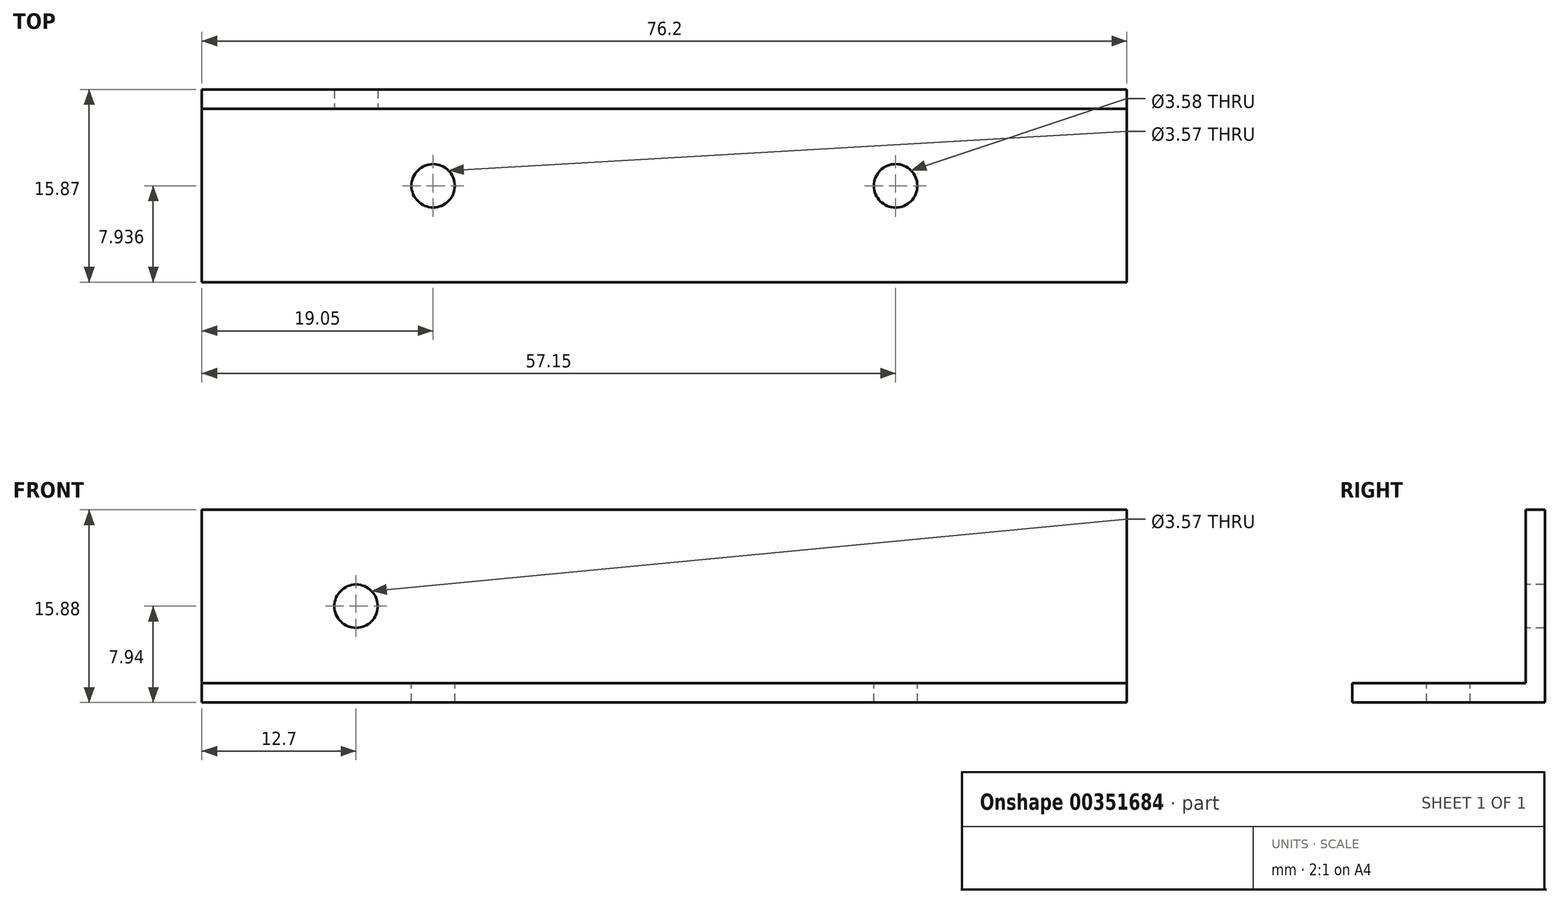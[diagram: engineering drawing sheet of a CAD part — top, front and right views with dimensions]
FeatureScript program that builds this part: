
annotation { "Feature Type Name" : "Feature", "Feature Type Description" : "" }
export const myFeature = defineFeature(function(context is Context, id is Id, definition is map)
    precondition{}
    {
        {
            var Q0;
            Q0=qCreatedBy(makeId("Front.planeOp"),FACE);
            var sketch = newSketch(context, id + "F0", { "sketchPlane" : qUnion([Q0])});
            skLineSegment(sketch, "E0.bottom", {"start": v(-38.1, 7.94) * mm, "end": v(38.1, 7.94) * mm});
            skLineSegment(sketch, "E0.top", {"start": v(-38.1, -7.94) * mm, "end": v(38.1, -7.94) * mm});
            skLineSegment(sketch, "E0.left", {"start": v(-38.1, 7.94) * mm, "end": v(-38.1, -7.94) * mm});
            skLineSegment(sketch, "E0.right", {"start": v(38.1, 7.94) * mm, "end": v(38.1, -7.94) * mm});
            skPoint(sketch, "E0.middle", {"position": v(0, 0) * mm});
            skSolve(sketch);
        }
        {
            var Q0;
            Q0 = qSketchRegion(id + "F0", true);
            extrude(context, id + "F1", {"entities" : qUnion([Q0]), "endBound" : BoundingType.SYMMETRIC, "depth" : 1.59 * mm});
        }
        {
            var Q0;
            Q0=makeQuery(id+"F1.opExtrude","CAP_FACE",FACE,{"disambiguationData":[OSD([sQuery(id+"F0.wireOp",EDGE,"E0.bottom"),sQuery(id+"F0.wireOp",EDGE,"E0.top"),sQuery(id+"F0.wireOp",EDGE,"E0.left"),sQuery(id+"F0.wireOp",EDGE,"E0.right")])],"isStart":false});
            var sketch = newSketch(context, id + "F2", { "sketchPlane" : qUnion([Q0])});
            skCircle(sketch, "E1", {"center": v(-25.4, 0) * mm, "radius": 1.79 * mm});
            skSolve(sketch);
        }
        {
            var Q0;
            Q0 = qSketchRegion(id + "F2", true);
            var Q1;
            Q1=makeQuery(id+"F1.opExtrude","CAP_FACE",FACE,{"disambiguationData":[OSD([sQuery(id+"F0.wireOp",EDGE,"E0.bottom"),sQuery(id+"F0.wireOp",EDGE,"E0.top"),sQuery(id+"F0.wireOp",EDGE,"E0.left"),sQuery(id+"F0.wireOp",EDGE,"E0.right")])],"isStart":true});
            extrude(context, id + "F3", {"entities" : qUnion([Q0]), "operationType" : NewBodyOperationType.REMOVE, "endBound" : BoundingType.UP_TO_SURFACE, "oppositeDirection" : true, "endBoundEntityFace" : qUnion([Q1]), "depth" : 25.4 * mm});
        }
        {
            var Q0;
            Q0=makeQuery(id+"F1.opExtrude","CAP_FACE",FACE,{"disambiguationData":[OSD([sQuery(id+"F0.wireOp",EDGE,"E0.bottom"),sQuery(id+"F0.wireOp",EDGE,"E0.top"),sQuery(id+"F0.wireOp",EDGE,"E0.left"),sQuery(id+"F0.wireOp",EDGE,"E0.right")])],"isStart":false});
            var sketch = newSketch(context, id + "F4", { "sketchPlane" : qUnion([Q0])});
            skLineSegment(sketch, "E2.bottom", {"start": v(-38.1, -7.94) * mm, "end": v(38.1, -7.94) * mm});
            skLineSegment(sketch, "E2.top", {"start": v(-38.1, -6.35) * mm, "end": v(38.1, -6.35) * mm});
            skLineSegment(sketch, "E2.left", {"start": v(-38.1, -7.94) * mm, "end": v(-38.1, -6.35) * mm});
            skLineSegment(sketch, "E2.right", {"start": v(38.1, -7.94) * mm, "end": v(38.1, -6.35) * mm});
            skSolve(sketch);
        }
        {
            var Q0;
            Q0 = qSketchRegion(id + "F4", true);
            extrude(context, id + "F5", {"entities" : qUnion([Q0]), "operationType" : NewBodyOperationType.ADD, "depth" : (15.88 * mm) - (1.59 * mm)});
        }
        {
            var Q0;
            Q0=makeQuery(id+"F5.opExtrude","SWEPT_FACE",FACE,{"disambiguationData":[OSD([sQuery(id+"F4.wireOp",EDGE,"E2.top")])]});
            var sketch = newSketch(context, id + "F6", { "sketchPlane" : qUnion([Q0])});
            skCircle(sketch, "E3", {"center": v(-19.05, -7.14) * mm, "radius": 1.79 * mm});
            skCircle(sketch, "E4", {"center": v(19.05, -7.14) * mm, "radius": 1.8 * mm});
            skSolve(sketch);
        }
        {
            var Q0;
            Q0 = qSketchRegion(id + "F6", true);
            var Q1;
            Q1=makeQuery(id+"F5.boolean.opBoolean","MERGE",FACE,{"derivedFrom":[makeQuery(id+"F1.opExtrude","SWEPT_FACE",FACE,{"disambiguationData":[OSD([sQuery(id+"F0.wireOp",EDGE,"E0.top")])]}),makeQuery(id+"F5.opExtrude","SWEPT_FACE",FACE,{"disambiguationData":[OSD([sQuery(id+"F4.wireOp",EDGE,"E2.bottom")])]})]});
            extrude(context, id + "F7", {"entities" : qUnion([Q0]), "operationType" : NewBodyOperationType.REMOVE, "endBound" : BoundingType.UP_TO_SURFACE, "oppositeDirection" : true, "endBoundEntityFace" : qUnion([Q1]), "depth" : 25.4 * mm});
        }
    });
